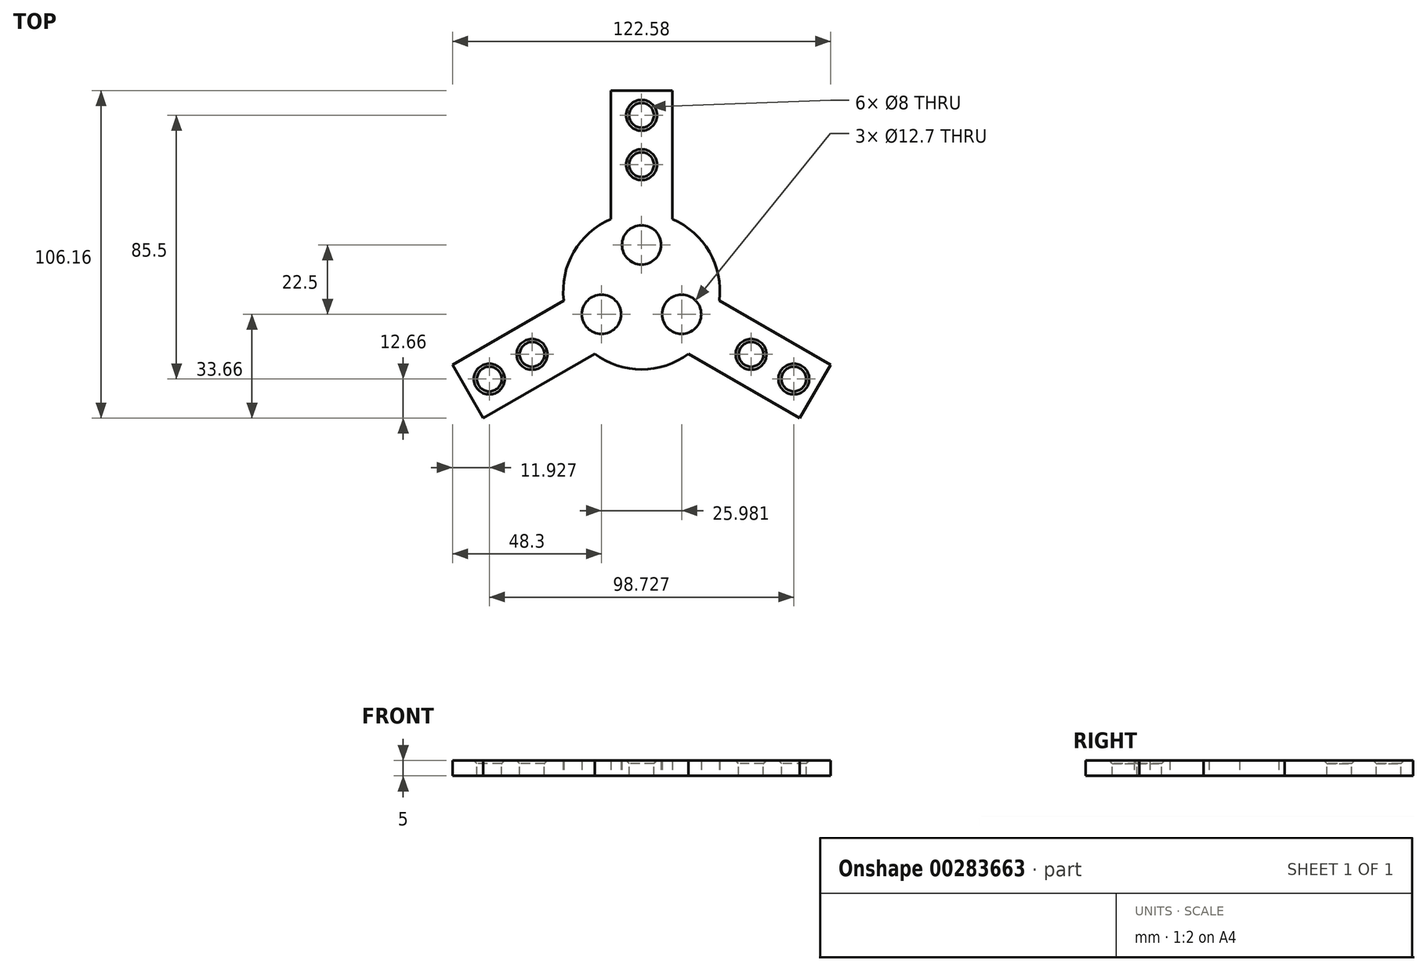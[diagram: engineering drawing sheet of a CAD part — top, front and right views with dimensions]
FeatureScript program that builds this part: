
annotation { "Feature Type Name" : "Feature", "Feature Type Description" : "" }
export const myFeature = defineFeature(function(context is Context, id is Id, definition is map)
    precondition{}
    {
        {
            var Q0;
            Q0=qCreatedBy(makeId("Top.planeOp"),FACE);
            var sketch = newSketch(context, id + "F0", { "sketchPlane" : qUnion([Q0])});
            skArc(sketch, "E0", {"start": v(-10, 23.35) * mm, "mid": v(-22, 12.7) * mm, "end": v(-25.22, -3.01) * mm});
            skCircle(sketch, "E1", {"center": v(0, 15) * mm, "radius": 6.35 * mm});
            skCircle(sketch, "E2.1.0", {"center": v(-13, -7.5) * mm, "radius": 6.35 * mm});
            skCircle(sketch, "E2.2.0", {"center": v(13, -7.5) * mm, "radius": 6.35 * mm});
            skLineSegment(sketch, "E3", {"start": v(-10, 23.35) * mm, "end": v(-10, 65) * mm});
            skLineSegment(sketch, "E4", {"start": v(-10, 65) * mm, "end": v(10, 65) * mm});
            skLineSegment(sketch, "E5", {"start": v(10, 65) * mm, "end": v(10, 23.35) * mm});
            skLineSegment(sketch, "E6", {"start": v(0, 15) * mm, "end": v(0, 65) * mm, "construction": true});
            skLineSegment(sketch, "E7.1.0", {"start": v(-15.22, -20.33) * mm, "end": v(-51.3, -41.16) * mm});
            skLineSegment(sketch, "E7.1.1", {"start": v(-51.3, -41.16) * mm, "end": v(-61.3, -23.84) * mm});
            skLineSegment(sketch, "E7.1.2", {"start": v(-61.3, -23.84) * mm, "end": v(-25.22, -3.01) * mm});
            skLineSegment(sketch, "E7.2.0", {"start": v(25.22, -3.01) * mm, "end": v(61.3, -23.84) * mm});
            skLineSegment(sketch, "E7.2.1", {"start": v(61.3, -23.84) * mm, "end": v(51.3, -41.16) * mm});
            skLineSegment(sketch, "E7.2.2", {"start": v(51.3, -41.16) * mm, "end": v(15.22, -20.33) * mm});
            skArc(sketch, "E8.trimOffspring", {"start": v(25.22, -3.01) * mm, "mid": v(22, 12.7) * mm, "end": v(10, 23.35) * mm});
            skArc(sketch, "E9.trimOffspring", {"start": v(-15.22, -20.33) * mm, "mid": v(0, -25.4) * mm, "end": v(15.22, -20.33) * mm});
            skSolve(sketch);
        }
        {
            var Q0;
            Q0=makeQuery(id+"F0.imprint","IMPRINT",FACE,{"disambiguationData":[TD([[makeQuery(id+"F0.imprint","IMPRINT",EDGE,{"derivedFrom":sQuery(id+"F0.wireOp",EDGE,"E0")}),1.0]])]});
            extrude(context, id + "F1", {"entities" : qUnion([Q0]), "depth" : 5 * mm});
        }
        {
            var Q0;
            Q0=makeQuery(id+"F1.opExtrude","CAP_FACE",FACE,{"disambiguationData":[OSD([sQuery(id+"F0.wireOp",EDGE,"E0"),sQuery(id+"F0.wireOp",EDGE,"E1"),sQuery(id+"F0.wireOp",EDGE,"E2.1.0"),sQuery(id+"F0.wireOp",EDGE,"E2.2.0"),sQuery(id+"F0.wireOp",EDGE,"E3"),sQuery(id+"F0.wireOp",EDGE,"E4"),sQuery(id+"F0.wireOp",EDGE,"E5"),sQuery(id+"F0.wireOp",EDGE,"E7.1.0"),sQuery(id+"F0.wireOp",EDGE,"E7.1.1"),sQuery(id+"F0.wireOp",EDGE,"E7.1.2"),sQuery(id+"F0.wireOp",EDGE,"E7.2.0"),sQuery(id+"F0.wireOp",EDGE,"E7.2.1"),sQuery(id+"F0.wireOp",EDGE,"E7.2.2"),sQuery(id+"F0.wireOp",EDGE,"E8.trimOffspring"),sQuery(id+"F0.wireOp",EDGE,"E9.trimOffspring")])],"isStart":false});
            var sketch = newSketch(context, id + "F2", { "sketchPlane" : qUnion([Q0])});
            skPoint(sketch, "E10", {"position": v(0, 57) * mm});
            skPoint(sketch, "E11", {"position": v(0, 41) * mm});
            skPoint(sketch, "E12.1.0", {"position": v(-49.36, -28.5) * mm});
            skPoint(sketch, "E12.1.1", {"position": v(-35.5, -20.5) * mm});
            skPoint(sketch, "E12.2.0", {"position": v(49.36, -28.5) * mm});
            skPoint(sketch, "E12.2.1", {"position": v(35.5, -20.5) * mm});
            skPoint(sketch, "E12.center", {"position": v(0, 0) * mm});
            skSolve(sketch);
        }
        {
            var Q0;
            Q0=sQuery(id+"F2.wireOp",VERTEX,"E10");
            var Q1;
            Q1=sQuery(id+"F2.wireOp",VERTEX,"E11");
            var Q2;
            Q2=sQuery(id+"F2.wireOp",VERTEX,"E12.2.1");
            var Q3;
            Q3=sQuery(id+"F2.wireOp",VERTEX,"E12.2.0");
            var Q4;
            Q4=sQuery(id+"F2.wireOp",VERTEX,"E12.1.1");
            var Q5;
            Q5=sQuery(id+"F2.wireOp",VERTEX,"E12.1.0");
            var Q6;
            Q6=makeQuery(id+"F1.opExtrude","SWEPT_BODY",BODY,{"disambiguationData":[OSD([sQuery(id+"F0.wireOp",EDGE,"E0"),sQuery(id+"F0.wireOp",EDGE,"E1"),sQuery(id+"F0.wireOp",EDGE,"E2.1.0"),sQuery(id+"F0.wireOp",EDGE,"E2.2.0"),sQuery(id+"F0.wireOp",EDGE,"E3"),sQuery(id+"F0.wireOp",EDGE,"E4"),sQuery(id+"F0.wireOp",EDGE,"E5"),sQuery(id+"F0.wireOp",EDGE,"E7.1.0"),sQuery(id+"F0.wireOp",EDGE,"E7.1.1"),sQuery(id+"F0.wireOp",EDGE,"E7.1.2"),sQuery(id+"F0.wireOp",EDGE,"E7.2.0"),sQuery(id+"F0.wireOp",EDGE,"E7.2.1"),sQuery(id+"F0.wireOp",EDGE,"E7.2.2"),sQuery(id+"F0.wireOp",EDGE,"E8.trimOffspring"),sQuery(id+"F0.wireOp",EDGE,"E9.trimOffspring")])]});
            hole(context, id + "F3", {"style" : HoleStyle.C_SINK, "endStyle" : HoleEndStyle.THROUGH, "holeDiameter" : 8 * mm, "cSinkDiameter" : 10 * mm, "cSinkAngle" : 90 * degree, "tappedDepth" : 12 * mm, "tapClearance" : 3, "locations" : qUnion([Q0, Q1, Q2, Q3, Q4, Q5]), "scope" : qUnion([Q6])});
        }
    });
